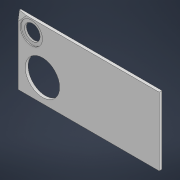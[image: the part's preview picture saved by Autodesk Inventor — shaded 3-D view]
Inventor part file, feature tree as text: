
AUTODESK INVENTOR PART (.ipt)
format: ipt  version: 2022 (Build 260153000, 153)  size: 131,584 bytes
history: native  units: mm
features: other x4, extrude x2, sketch x1
ambient origin geometry x8: Origin, YZ Plane, XZ Plane, XY Plane, X Axis, Y Axis, Z Axis, Center Point
bodies: Body1 (feature_tree)
feature tree (7):
  other  "Твердое тело1"
  other  "Front0"
  extrude  "Выдавливание2"  Depth=600.0mm
  other  "РабПлоскость9"
  other  "Разделение5"
  extrude  "Выдавливание7"  Depth=290.0mm
  sketch  "Эскиз7"
